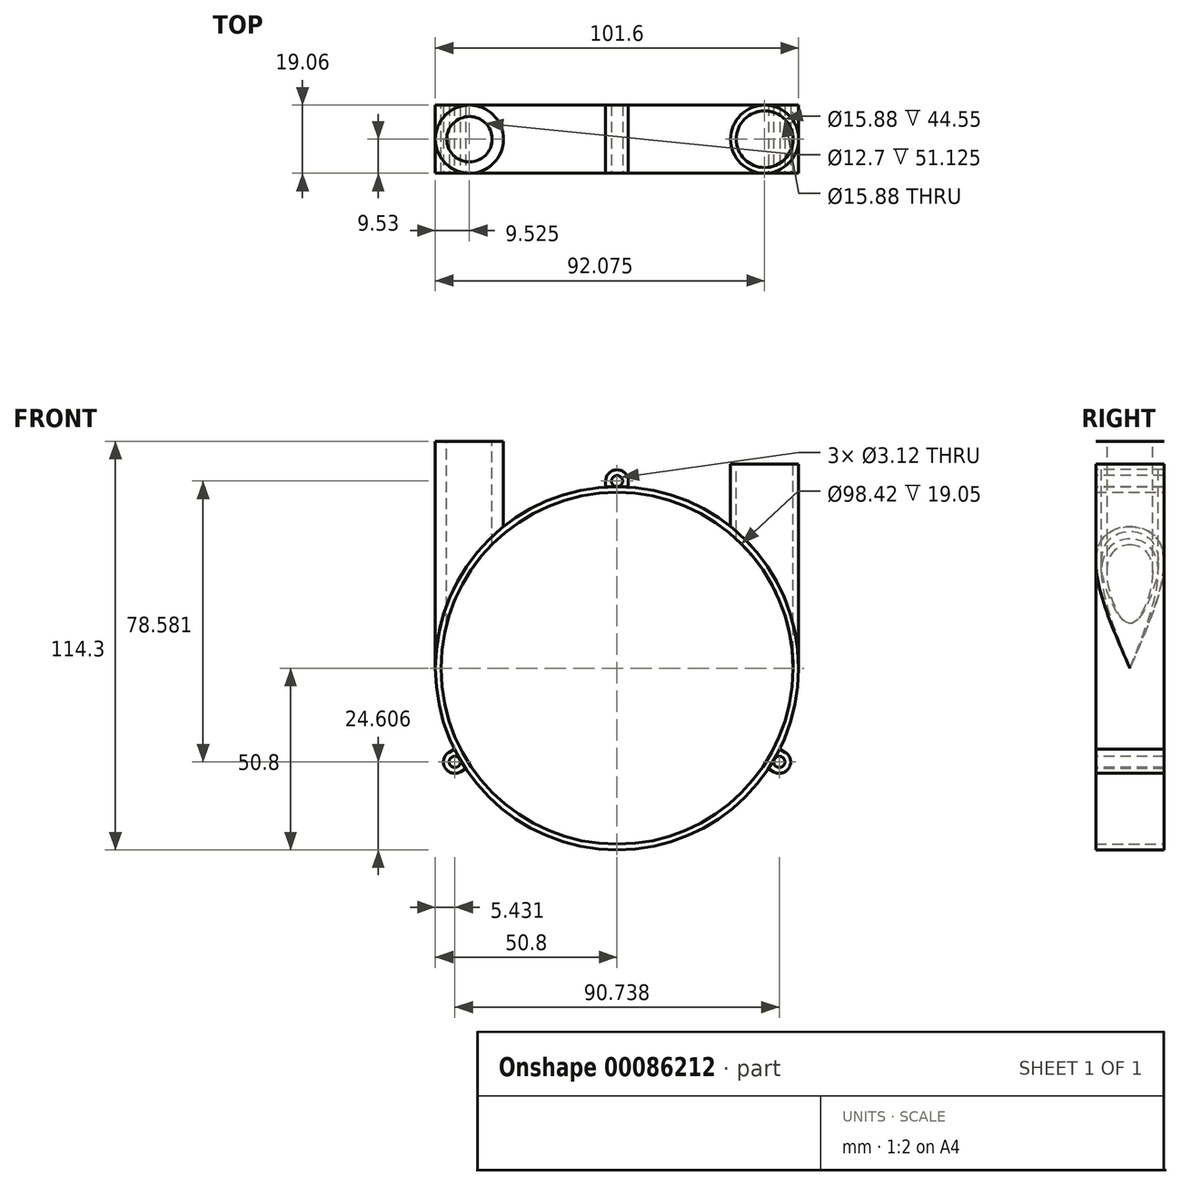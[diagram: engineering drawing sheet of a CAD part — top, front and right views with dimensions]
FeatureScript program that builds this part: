
annotation { "Feature Type Name" : "Feature", "Feature Type Description" : "" }
export const myFeature = defineFeature(function(context is Context, id is Id, definition is map)
    precondition{}
    {
        {
            var Q0;
            Q0=qCreatedBy(makeId("Front.planeOp"),FACE);
            var sketch = newSketch(context, id + "F0", { "sketchPlane" : qUnion([Q0])});
            skArc(sketch, "E0", {"start": v(-50.8, 0) * mm, "mid": v(0, -50.8) * mm, "end": v(50.8, 0) * mm});
            skArc(sketch, "E1.trimOffspring", {"start": v(50.8, 0) * mm, "mid": v(0, 50.8) * mm, "end": v(-50.8, 0) * mm});
            skSolve(sketch);
        }
        {
            var Q0;
            Q0=makeQuery(id+"F0.imprint","IMPRINT",FACE,{"disambiguationData":[TD([[makeQuery(id+"F0.imprint","IMPRINT",EDGE,{"derivedFrom":sQuery(id+"F0.wireOp",EDGE,"E0")}),1.0]])]});
            extrude(context, id + "F1", {"entities" : qUnion([Q0]), "endBound" : BoundingType.SYMMETRIC, "depth" : 19.05 * mm});
        }
        {
            var Q0;
            Q0=makeQuery(id+"F1.opExtrude","CAP_FACE",FACE,{"disambiguationData":[OSD([sQuery(id+"F0.wireOp",EDGE,"E0"),sQuery(id+"F0.wireOp",EDGE,"PEXug1yW-JhST-EnxC-8VC1-HZBpnZdRSoe1"),sQuery(id+"F0.wireOp",EDGE,"QBzd2IPM-GnY9-3ujY-iMRs-ao6Hw2nljluK"),sQuery(id+"F0.wireOp",EDGE,"xjxUBAig-dIdY-odEl-2dFv-ZXaTAuvfei7t"),sQuery(id+"F0.wireOp",EDGE,"BbE9P5Mz-f3yn-frGt-81af-cIKdAYjhxu96"),sQuery(id+"F0.wireOp",EDGE,"s7lU5Rhb-QI50-guGO-FJX9-CQGfkjgQxZ08"),sQuery(id+"F0.wireOp",EDGE,"XQ8alRdB-VkET-ZBQC-aipF-n0BgqIxJT99B"),sQuery(id+"F0.wireOp",EDGE,"E1.trimOffspring")])],"isStart":true});
            var sketch = newSketch(context, id + "F2", { "sketchPlane" : qUnion([Q0])});
            skCircle(sketch, "E2", {"center": v(0, 0) * mm, "radius": 49.21 * mm});
            skSolve(sketch);
        }
        {
            var Q0;
            Q0 = qSketchRegion(id + "F2", true);
            extrude(context, id + "F3", {"entities" : qUnion([Q0]), "operationType" : NewBodyOperationType.REMOVE, "oppositeDirection" : true, "depth" : 25.4 * mm});
        }
        {
            var Q0;
            Q0=qCreatedBy(makeId("Top.planeOp"),FACE);
            cPlane(context, id + "F4", {"entities" : qUnion([Q0]), "cplaneType" : CPlaneType.OFFSET, "offset" : 63.5 * mm, "width" : 152.4 * mm, "height" : 152.4 * mm});
        }
        {
            var Q0;
            Q0=qCreatedBy(id+"F4.planeOp",FACE);
            var sketch = newSketch(context, id + "F5", { "sketchPlane" : qUnion([Q0])});
            skCircle(sketch, "E3", {"center": v(-41.28, 0) * mm, "radius": 9.53 * mm});
            skSolve(sketch);
        }
        {
            var Q0;
            Q0 = qSketchRegion(id + "F5", true);
            extrude(context, id + "F6", {"entities" : qUnion([Q0]), "operationType" : NewBodyOperationType.ADD, "endBound" : BoundingType.UP_TO_NEXT, "oppositeDirection" : true, "depth" : 25.4 * mm});
        }
        {
            var Q0;
            Q0=qCreatedBy(makeId("Top.planeOp"),FACE);
            cPlane(context, id + "F7", {"entities" : qUnion([Q0]), "cplaneType" : CPlaneType.OFFSET, "offset" : 57.15 * mm, "width" : 152.4 * mm, "height" : 152.4 * mm});
        }
        {
            var Q0;
            Q0=qCreatedBy(id+"F7.planeOp",FACE);
            var sketch = newSketch(context, id + "F8", { "sketchPlane" : qUnion([Q0])});
            skCircle(sketch, "E4", {"center": v(41.28, 0) * mm, "radius": 9.53 * mm});
            skSolve(sketch);
        }
        {
            var Q0;
            Q0 = qSketchRegion(id + "F8", true);
            extrude(context, id + "F9", {"entities" : qUnion([Q0]), "endBound" : BoundingType.UP_TO_NEXT, "oppositeDirection" : true, "depth" : 25.4 * mm});
        }
        {
            var Q0;
            Q0=makeQuery(id+"F6.opExtrude","CAP_FACE",FACE,{"disambiguationData":[OSD([sQuery(id+"F5.wireOp",EDGE,"E3")])],"isStart":true});
            var sketch = newSketch(context, id + "F10", { "sketchPlane" : qUnion([Q0])});
            skCircle(sketch, "E5", {"center": v(-41.28, 0) * mm, "radius": 6.35 * mm});
            skCircle(sketch, "E6", {"center": v(41.28, 0) * mm, "radius": 7.94 * mm});
            skSolve(sketch);
        }
        {
            var Q0;
            Q0 = qSketchRegion(id + "F10", true);
            var Q1;
            Q1=makeQuery(id+"F3.boolean.opBoolean","COPY",FACE,{"derivedFrom":makeQuery(id+"F3.opExtrude","SWEPT_FACE",FACE,{"disambiguationData":[OSD([sQuery(id+"F2.wireOp",EDGE,"E2")])]})});
            extrude(context, id + "F11", {"entities" : qUnion([Q0]), "operationType" : NewBodyOperationType.REMOVE, "oppositeDirection" : true, "endBoundEntityFace" : qUnion([Q1]), "depth" : 63.5 * mm});
        }
        {
            var Q0;
            Q0=makeQuery(id+"F1.opExtrude","CAP_FACE",FACE,{"disambiguationData":[OSD([sQuery(id+"F0.wireOp",EDGE,"E0"),sQuery(id+"F0.wireOp",EDGE,"E1.trimOffspring")])],"isStart":false});
            var sketch = newSketch(context, id + "F12", { "sketchPlane" : qUnion([Q0])});
            skCircle(sketch, "E7", {"center": v(0, 52.39) * mm, "radius": 1.56 * mm});
            skLineSegment(sketch, "E8", {"start": v(-3.18, 50.7) * mm, "end": v(-3.18, 52.39) * mm});
            skLineSegment(sketch, "E9", {"start": v(3.18, 50.7) * mm, "end": v(3.18, 52.39) * mm});
            skArc(sketch, "E10", {"start": v(3.18, 52.39) * mm, "mid": v(0, 55.56) * mm, "end": v(-3.18, 52.39) * mm});
            skArc(sketch, "E11", {"start": v(3.17, 50.7) * mm, "mid": v(0, 50.8) * mm, "end": v(-3.18, 50.7) * mm});
            skArc(sketch, "E12.1.0", {"start": v(-46.96, -23.44) * mm, "mid": v(-48.12, -27.78) * mm, "end": v(-43.78, -28.94) * mm});
            skArc(sketch, "E12.1.1", {"start": v(-45.5, -22.6) * mm, "mid": v(-44, -25.4) * mm, "end": v(-42.32, -28.1) * mm});
            skCircle(sketch, "E12.1.2", {"center": v(-45.37, -26.2) * mm, "radius": 1.56 * mm});
            skLineSegment(sketch, "E12.1.3", {"start": v(-45.5, -22.6) * mm, "end": v(-46.96, -23.44) * mm});
            skLineSegment(sketch, "E12.1.4", {"start": v(-42.32, -28.1) * mm, "end": v(-43.78, -28.94) * mm});
            skArc(sketch, "E12.2.0", {"start": v(43.78, -28.94) * mm, "mid": v(48.12, -27.78) * mm, "end": v(46.96, -23.44) * mm});
            skArc(sketch, "E12.2.1", {"start": v(42.32, -28.1) * mm, "mid": v(44, -25.4) * mm, "end": v(45.5, -22.6) * mm});
            skCircle(sketch, "E12.2.2", {"center": v(45.37, -26.2) * mm, "radius": 1.56 * mm});
            skLineSegment(sketch, "E12.2.3", {"start": v(42.32, -28.1) * mm, "end": v(43.78, -28.94) * mm});
            skLineSegment(sketch, "E12.2.4", {"start": v(45.5, -22.6) * mm, "end": v(46.96, -23.44) * mm});
            skSolve(sketch);
        }
        {
            var Q0;
            {var subQ3=sQuery(id+"F12.wireOp",EDGE,"E7");Q0=makeQuery(id+"F12.imprint","IMPRINT",FACE,{"disambiguationData":[TD([[makeQuery(id+"F12.imprint","IMPRINT",EDGE,{"derivedFrom":subQ3}),-1.0]])]});}
            var Q1;
            Q1=makeQuery(id+"F12.imprint","IMPRINT",FACE,{"disambiguationData":[TD([[makeQuery(id+"F12.imprint","IMPRINT",EDGE,{"derivedFrom":sQuery(id+"F12.wireOp",EDGE,"E12.2.0")}),1.0]])]});
            var Q2;
            Q2=makeQuery(id+"F12.imprint","IMPRINT",FACE,{"disambiguationData":[TD([[makeQuery(id+"F12.imprint","IMPRINT",EDGE,{"derivedFrom":sQuery(id+"F12.wireOp",EDGE,"E12.1.0")}),1.0]])]});
            extrude(context, id + "F13", {"entities" : qUnion([Q0, Q1, Q2]), "oppositeDirection" : true, "depth" : 19.05 * mm});
        }
    });
